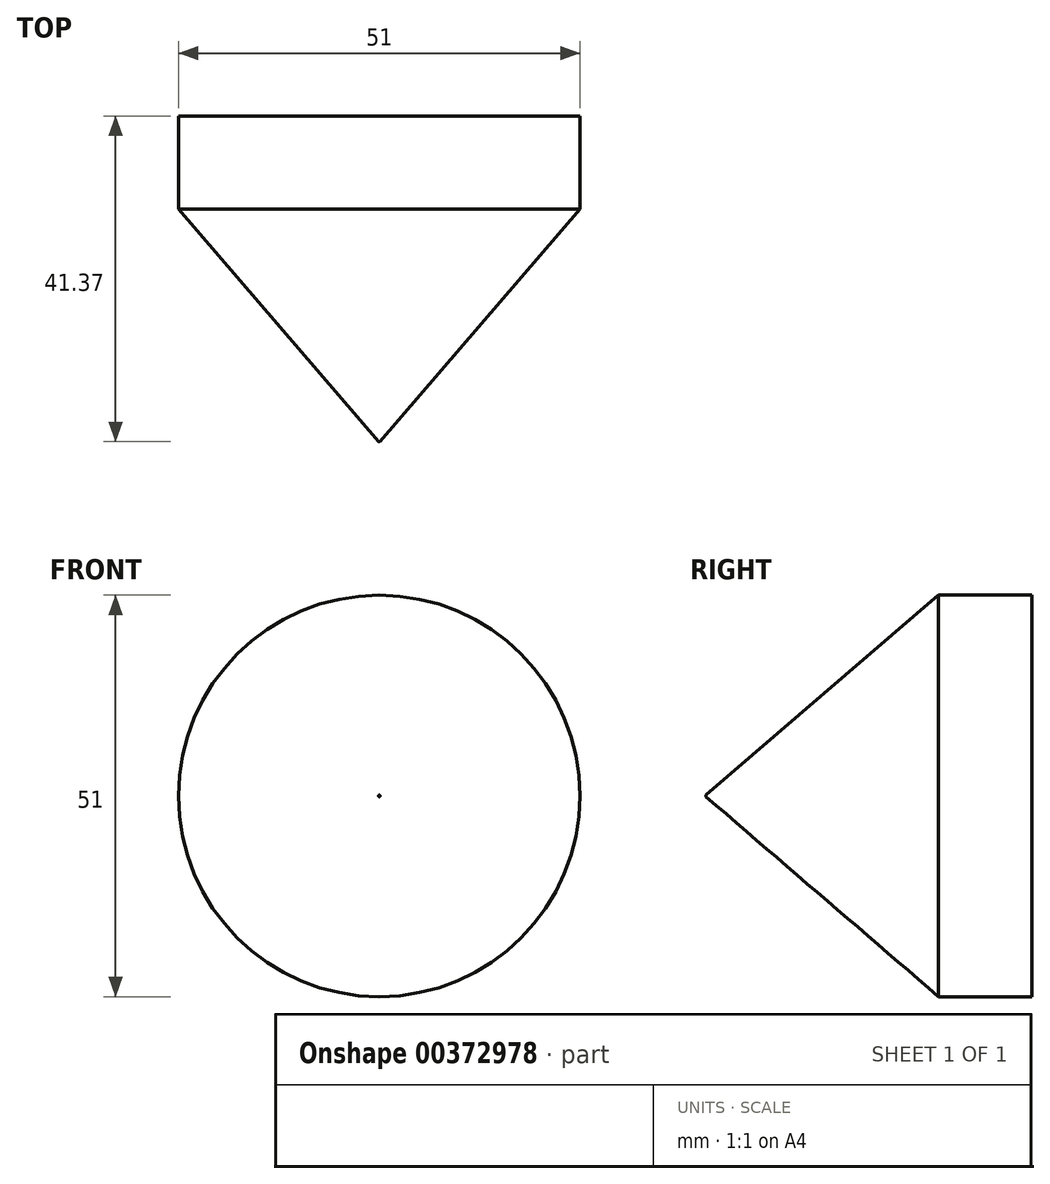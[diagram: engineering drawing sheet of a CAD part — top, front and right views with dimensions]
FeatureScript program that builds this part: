
annotation { "Feature Type Name" : "Feature", "Feature Type Description" : "" }
export const myFeature = defineFeature(function(context is Context, id is Id, definition is map)
    precondition{}
    {
        {
            var Q0;
            Q0=qCreatedBy(makeId("Top.planeOp"),FACE);
            var sketch = newSketch(context, id + "F0", { "sketchPlane" : qUnion([Q0])});
            skLineSegment(sketch, "E0.bottom", {"start": v(0, 0) * mm, "end": v(36, 0) * mm, "construction": true});
            skLineSegment(sketch, "E0.top", {"start": v(0, 24) * mm, "end": v(36, 24) * mm, "construction": true});
            skLineSegment(sketch, "E0.left", {"start": v(0, 0) * mm, "end": v(0, 24) * mm, "construction": true});
            skLineSegment(sketch, "E0.right", {"start": v(36, 0) * mm, "end": v(36, 24) * mm, "construction": true});
            skLineSegment(sketch, "E1", {"start": v(18, 24) * mm, "end": v(18, 12) * mm, "construction": true});
            skPoint(sketch, "E1.endSnap0", {"position": v(36, 12) * mm});
            skLineSegment(sketch, "E2", {"start": v(18, 12) * mm, "end": v(36, 12) * mm, "construction": true});
            skLineSegment(sketch, "E3", {"start": v(18, 12) * mm, "end": v(36, 24) * mm, "construction": true});
            skLineSegment(sketch, "E4", {"start": v(-52.27, 0) * mm, "end": v(-52.27, 29.55) * mm});
            skLineSegment(sketch, "E5", {"start": v(-52.27, 29.55) * mm, "end": v(-26.77, 29.55) * mm, "construction": true});
            skLineSegment(sketch, "E6", {"start": v(-52.27, 29.55) * mm, "end": v(-52.27, 41.37) * mm});
            skLineSegment(sketch, "E7", {"start": v(-52.27, 41.37) * mm, "end": v(-26.77, 41.37) * mm});
            skLineSegment(sketch, "E8", {"start": v(-26.77, 41.37) * mm, "end": v(-26.77, 29.55) * mm});
            skLineSegment(sketch, "E9", {"start": v(-26.77, 29.55) * mm, "end": v(-52.17, 0) * mm});
            skLineSegment(sketch, "E10", {"start": v(-52.17, 0) * mm, "end": v(-52.27, 0) * mm});
            skLineSegment(sketch, "E11", {"start": v(-52.27, 0) * mm, "end": v(-52.27, -12.06) * mm, "construction": true});
            skSolve(sketch);
        }
        {
            var Q0;
            Q0 = qSketchRegion(id + "F0", true);
            var Q1;
            Q1=sQuery(id+"F0.wireOp",EDGE,"E6");
            revolve(context, id + "F1", {"entities" : qUnion([Q0]), "axis" : qUnion([Q1]), "revolveType" : RevolveType.FULL});
        }
    });
